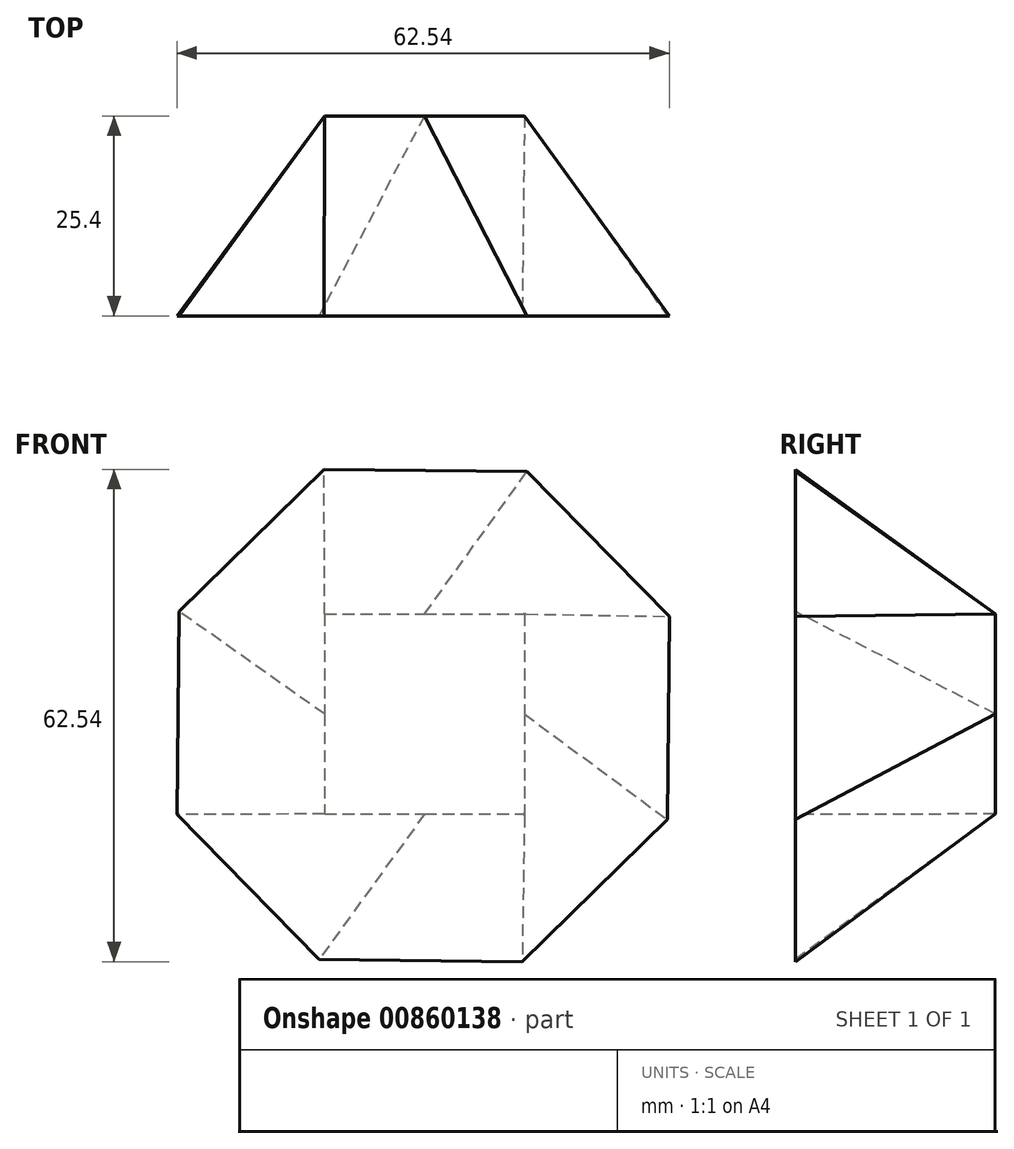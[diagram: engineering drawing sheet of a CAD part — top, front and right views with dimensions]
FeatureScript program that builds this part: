
annotation { "Feature Type Name" : "Feature", "Feature Type Description" : "" }
export const myFeature = defineFeature(function(context is Context, id is Id, definition is map)
    precondition{}
    {
        {
            var Q0;
            Q0=qCreatedBy(makeId("Front.planeOp"),FACE);
            var sketch = newSketch(context, id + "F0", { "sketchPlane" : qUnion([Q0])});
            skLineSegment(sketch, "E0.bottom", {"start": v(-12.52, 12.88) * mm, "end": v(12.88, 12.88) * mm});
            skLineSegment(sketch, "E0.top", {"start": v(-12.52, -12.52) * mm, "end": v(12.88, -12.52) * mm});
            skLineSegment(sketch, "E0.left", {"start": v(-12.52, 12.88) * mm, "end": v(-12.52, -12.52) * mm});
            skLineSegment(sketch, "E0.right", {"start": v(12.88, 12.88) * mm, "end": v(12.88, -12.52) * mm});
            skLineSegment(sketch, "E1", {"start": v(0, 57.9) * mm, "end": v(0, -57.44) * mm, "construction": true});
            skLineSegment(sketch, "E2", {"start": v(0, 0) * mm, "end": v(12.88, 12.88) * mm, "construction": true});
            skSolve(sketch);
        }
        {
            var Q0;
            Q0=qCreatedBy(makeId("Front.planeOp"),FACE);
            cPlane(context, id + "F1", {"entities" : qUnion([Q0]), "cplaneType" : CPlaneType.OFFSET, "offset" : 25.4 * mm, "width" : 152.4 * mm, "height" : 152.4 * mm});
        }
        {
            var Q0;
            Q0=qCreatedBy(id+"F1.planeOp",FACE);
            var sketch = newSketch(context, id + "F2", { "sketchPlane" : qUnion([Q0])});
            skCircle(sketch, "E3.cCircle", {"center": v(0, 0) * mm, "radius": 31.14 * mm, "construction": true});
            skLineSegment(sketch, "E3.0", {"start": v(-13.22, -31) * mm, "end": v(-31.27, -12.58) * mm});
            skLineSegment(sketch, "E3.1", {"start": v(-31.27, -12.58) * mm, "end": v(-31, 13.22) * mm});
            skLineSegment(sketch, "E3.2", {"start": v(-31, 13.22) * mm, "end": v(-12.58, 31.27) * mm});
            skLineSegment(sketch, "E3.3", {"start": v(-12.58, 31.27) * mm, "end": v(13.22, 31) * mm});
            skLineSegment(sketch, "E3.4", {"start": v(13.22, 31) * mm, "end": v(31.27, 12.58) * mm});
            skLineSegment(sketch, "E3.5", {"start": v(31.27, 12.58) * mm, "end": v(31, -13.22) * mm});
            skLineSegment(sketch, "E3.6", {"start": v(31, -13.22) * mm, "end": v(12.58, -31.27) * mm});
            skLineSegment(sketch, "E3.7", {"start": v(12.58, -31.27) * mm, "end": v(-13.22, -31) * mm});
            skPoint(sketch, "E3.0.midPoint", {"position": v(-22.25, -21.8) * mm});
            skSolve(sketch);
        }
        {
            var Q0;
            Q0=makeQuery(id+"F0.imprint","IMPRINT",FACE,{"disambiguationData":[TD([[makeQuery(id+"F0.imprint","IMPRINT",EDGE,{"derivedFrom":sQuery(id+"F0.wireOp",EDGE,"E0.bottom")}),-1.0]])]});
            var Q1;
            Q1=makeQuery(id+"F2.imprint","IMPRINT",FACE,{"disambiguationData":[TD([[makeQuery(id+"F2.imprint","IMPRINT",EDGE,{"derivedFrom":sQuery(id+"F2.wireOp",EDGE,"E3.0")}),-1.0]])]});
            loft(context, id + "F3", {"sheetProfilesArray" : [{ "sheetProfileEntities" : qUnion([Q0]) }, { "sheetProfileEntities" : qUnion([Q1]) }]});
        }
    });
